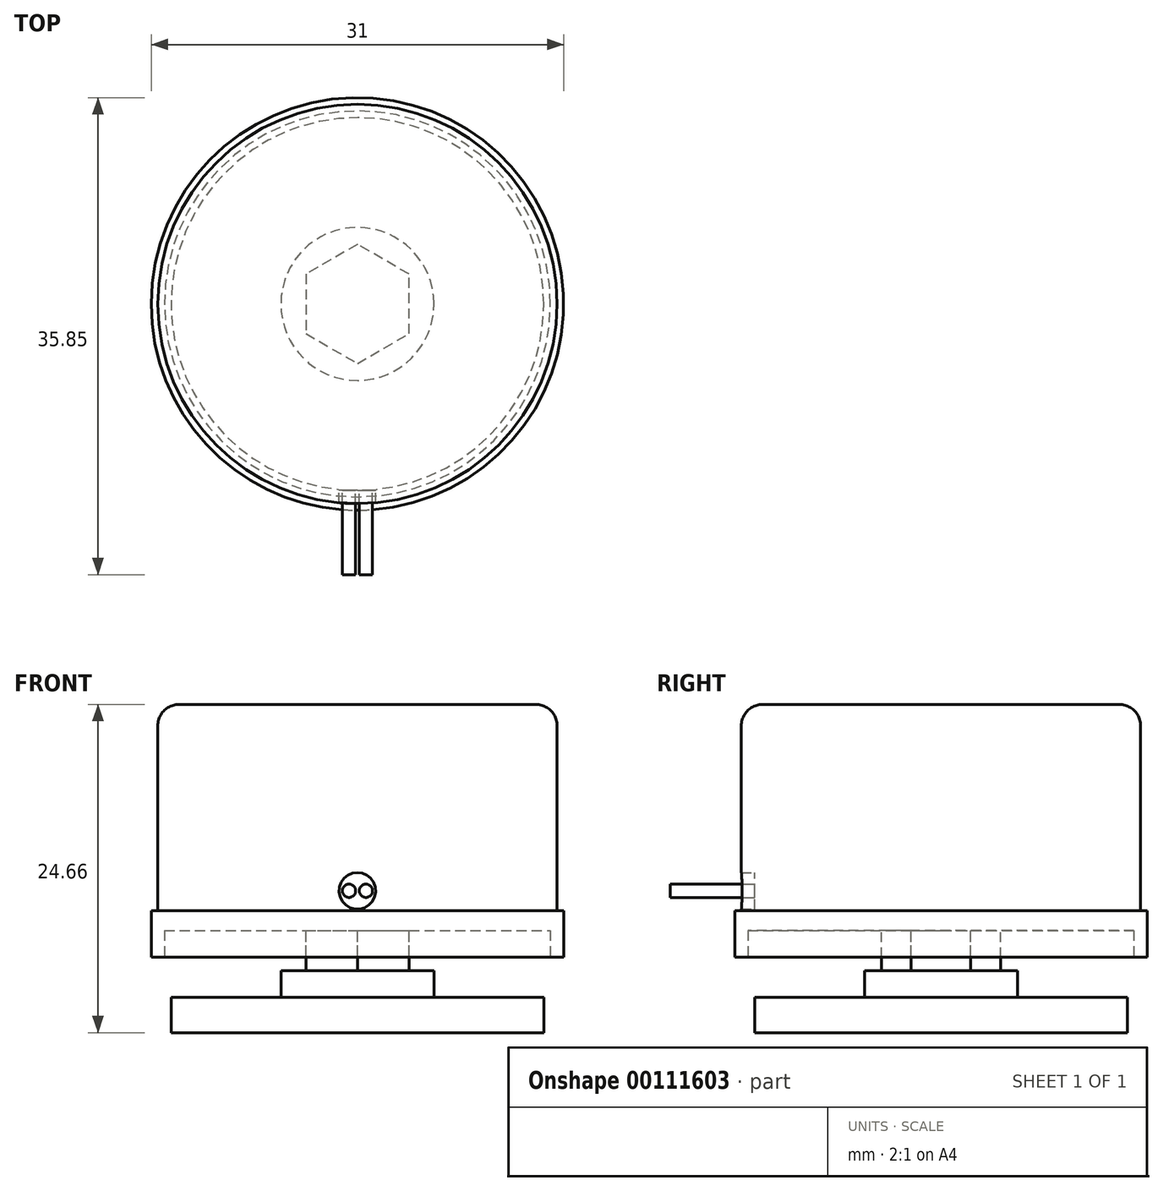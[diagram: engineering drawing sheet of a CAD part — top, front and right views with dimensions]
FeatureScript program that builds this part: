
annotation { "Feature Type Name" : "Feature", "Feature Type Description" : "" }
export const myFeature = defineFeature(function(context is Context, id is Id, definition is map)
    precondition{}
    {
        {
            var Q0;
            Q0=qCreatedBy(makeId("Top.planeOp"),FACE);
            var sketch = newSketch(context, id + "F0", { "sketchPlane" : qUnion([Q0])});
            skCircle(sketch, "E0", {"center": v(0, 0) * mm, "radius": 15 * mm});
            skSolve(sketch);
        }
        {
            var Q0;
            Q0 = qSketchRegion(id + "F0", true);
            extrude(context, id + "F1", {"entities" : qUnion([Q0]), "depth" : 19 * mm});
        }
        {
            var Q0;
            Q0=makeQuery(id+"F1.opExtrude","CAP_EDGE",EDGE,{"disambiguationData":[OSD([sQuery(id+"F0.wireOp",EDGE,"E0")])],"isStart":false});
            fillet(context, id + "F2", {"entities" : qUnion([Q0]), "radius" : 1.59 * mm, "tangentPropagation" : true, "allowEdgeOverflow" : false});
        }
        {
            var Q0;
            Q0=makeQuery(id+"F1.opExtrude","CAP_FACE",FACE,{"disambiguationData":[OSD([sQuery(id+"F0.wireOp",EDGE,"E0")])],"isStart":true});
            var sketch = newSketch(context, id + "F3", { "sketchPlane" : qUnion([Q0])});
            skCircle(sketch, "E1", {"center": v(0, 0) * mm, "radius": 15.5 * mm});
            skSolve(sketch);
        }
        {
            var Q0;
            Q0=makeQuery(id+"F3.imprint","IMPRINT",FACE,{"disambiguationData":[TD([[makeQuery(id+"F3.imprint","IMPRINT",EDGE,{"derivedFrom":sQuery(id+"F3.wireOp",EDGE,"E1")}),1.0]])]});
            extrude(context, id + "F4", {"entities" : qUnion([Q0]), "operationType" : NewBodyOperationType.ADD, "oppositeDirection" : true, "depth" : 3.5 * mm});
        }
        {
            var Q0;
            {var subQ0=sQuery(id+"F0.wireOp",EDGE,"E0");Q0=makeQuery(id+"F4.boolean.opBoolean","MERGE",FACE,{"derivedFrom":[makeQuery(id+"F1.opExtrude","CAP_FACE",FACE,{"disambiguationData":[OSD([subQ0])],"isStart":true}),makeQuery(id+"F4.opExtrude","CAP_FACE",FACE,{"disambiguationData":[OSD([subQ0,sQuery(id+"F3.wireOp",EDGE,"E1")])],"isStart":true})]});}
            var sketch = newSketch(context, id + "F5", { "sketchPlane" : qUnion([Q0])});
            skCircle(sketch, "E2", {"center": v(0, 0) * mm, "radius": 14.5 * mm});
            skSolve(sketch);
        }
        {
            var Q0;
            Q0=makeQuery(id+"F5.imprint","IMPRINT",FACE,{"disambiguationData":[TD([[makeQuery(id+"F5.imprint","IMPRINT",EDGE,{"derivedFrom":sQuery(id+"F5.wireOp",EDGE,"E2")}),1.0]])]});
            extrude(context, id + "F6", {"entities" : qUnion([Q0]), "operationType" : NewBodyOperationType.REMOVE, "oppositeDirection" : true, "depth" : 2 * mm});
        }
        {
            var Q0;
            Q0=makeQuery(id+"F6.boolean.opBoolean","COPY",FACE,{"derivedFrom":makeQuery(id+"F6.opExtrude","CAP_FACE",FACE,{"disambiguationData":[OSD([sQuery(id+"F5.wireOp",EDGE,"E2")])],"isStart":false})});
            var sketch = newSketch(context, id + "F7", { "sketchPlane" : qUnion([Q0])});
            skCircle(sketch, "E3.cCircle", {"center": v(0, 0) * mm, "radius": 3.88 * mm, "construction": true});
            skLineSegment(sketch, "E3.0", {"start": v(-3.87, 2.24) * mm, "end": v(0, 4.47) * mm});
            skLineSegment(sketch, "E3.1", {"start": v(0, 4.47) * mm, "end": v(3.88, 2.24) * mm});
            skLineSegment(sketch, "E3.2", {"start": v(3.88, 2.24) * mm, "end": v(3.88, -2.24) * mm});
            skLineSegment(sketch, "E3.3", {"start": v(3.88, -2.24) * mm, "end": v(0, -4.47) * mm});
            skLineSegment(sketch, "E3.4", {"start": v(0, -4.47) * mm, "end": v(-3.88, -2.24) * mm});
            skLineSegment(sketch, "E3.5", {"start": v(-3.88, -2.24) * mm, "end": v(-3.87, 2.24) * mm});
            skPoint(sketch, "E3.0.midPoint", {"position": v(-1.94, 3.36) * mm});
            skSolve(sketch);
        }
        {
            var Q0;
            Q0=makeQuery(id+"F7.imprint","IMPRINT",FACE,{"disambiguationData":[TD([[makeQuery(id+"F7.imprint","IMPRINT",EDGE,{"derivedFrom":sQuery(id+"F7.wireOp",EDGE,"E3.0")}),-1.0]])]});
            extrude(context, id + "F8", {"entities" : qUnion([Q0]), "operationType" : NewBodyOperationType.ADD, "depth" : 3 * mm});
        }
        {
            var Q0;
            Q0=makeQuery(id+"F8.opExtrude","CAP_FACE",FACE,{"disambiguationData":[OSD([sQuery(id+"F7.wireOp",EDGE,"E3.0"),sQuery(id+"F7.wireOp",EDGE,"E3.1"),sQuery(id+"F7.wireOp",EDGE,"E3.2"),sQuery(id+"F7.wireOp",EDGE,"E3.3"),sQuery(id+"F7.wireOp",EDGE,"E3.4"),sQuery(id+"F7.wireOp",EDGE,"E3.5")])],"isStart":false});
            var sketch = newSketch(context, id + "F9", { "sketchPlane" : qUnion([Q0])});
            skCircle(sketch, "E4", {"center": v(0, 0) * mm, "radius": 5.75 * mm});
            skSolve(sketch);
        }
        {
            var Q0;
            Q0=makeQuery(id+"F9.imprint","IMPRINT",FACE,{"disambiguationData":[TD([[makeQuery(id+"F9.imprint","IMPRINT",EDGE,{"derivedFrom":makeQuery(id+"F8.opExtrude","CAP_EDGE",EDGE,{"disambiguationData":[OSD([sQuery(id+"F7.wireOp",EDGE,"E3.0")])],"isStart":false})}),-1.0]])]});
            var Q1;
            Q1=makeQuery(id+"F9.imprint","IMPRINT",FACE,{"disambiguationData":[TD([[makeQuery(id+"F9.imprint","IMPRINT",EDGE,{"derivedFrom":sQuery(id+"F9.wireOp",EDGE,"E4")}),1.0]])]});
            extrude(context, id + "F10", {"entities" : qUnion([Q0, Q1]), "operationType" : NewBodyOperationType.ADD, "depth" : 2 * mm});
        }
        {
            var Q0;
            Q0=makeQuery(id+"F10.opExtrude","CAP_FACE",FACE,{"disambiguationData":[OSD([sQuery(id+"F9.wireOp",EDGE,"E4")])],"isStart":false});
            var sketch = newSketch(context, id + "F11", { "sketchPlane" : qUnion([Q0])});
            skCircle(sketch, "E5", {"center": v(0, 0) * mm, "radius": 14 * mm});
            skSolve(sketch);
        }
        {
            var Q0;
            Q0=makeQuery(id+"F11.imprint","IMPRINT",FACE,{"disambiguationData":[TD([[makeQuery(id+"F11.imprint","IMPRINT",EDGE,{"derivedFrom":sQuery(id+"F11.wireOp",EDGE,"E5")}),1.0]])]});
            var Q1;
            Q1=makeQuery(id+"F11.imprint","IMPRINT",FACE,{"disambiguationData":[TD([[makeQuery(id+"F11.imprint","IMPRINT",EDGE,{"derivedFrom":makeQuery(id+"F10.opExtrude","CAP_EDGE",EDGE,{"disambiguationData":[OSD([sQuery(id+"F9.wireOp",EDGE,"E4")])],"isStart":false})}),1.0]])]});
            extrude(context, id + "F12", {"entities" : qUnion([Q0, Q1]), "operationType" : NewBodyOperationType.ADD, "depth" : 2.66 * mm});
        }
        {
            var Q0;
            Q0=qCreatedBy(makeId("Front.planeOp"),FACE);
            var sketch = newSketch(context, id + "F13", { "sketchPlane" : qUnion([Q0])});
            skCircle(sketch, "E6", {"center": v(0, 5) * mm, "radius": 1.38 * mm});
            skSolve(sketch);
        }
        {
            var Q0;
            Q0 = qSketchRegion(id + "F13", true);
            extrude(context, id + "F14", {"entities" : qUnion([Q0]), "operationType" : NewBodyOperationType.REMOVE, "depth" : 25.4 * mm, "hasSecondDirection" : true, "secondDirectionOppositeDirection" : false, "secondDirectionDepth" : 14 * mm});
        }
        {
            var Q0;
            Q0=makeQuery(id+"F14.boolean.opBoolean","COPY",FACE,{"derivedFrom":makeQuery(id+"F14.opExtrude","CAP_FACE",FACE,{"disambiguationData":[OSD([sQuery(id+"F13.wireOp",EDGE,"E6")])],"isStart":true})});
            var sketch = newSketch(context, id + "F15", { "sketchPlane" : qUnion([Q0])});
            skCircle(sketch, "E7", {"center": v(-0.64, 5) * mm, "radius": 0.5 * mm});
            skCircle(sketch, "E8", {"center": v(0.63, 5) * mm, "radius": 0.5 * mm});
            skCircle(sketch, "E9.0", {"center": v(0, 5) * mm, "radius": 1.38 * mm});
            skLineSegment(sketch, "E10", {"start": v(-0.64, 5) * mm, "end": v(0.63, 5) * mm, "construction": true});
            skSolve(sketch);
        }
        {
            var Q0;
            Q0=makeQuery(id+"F15.imprint","IMPRINT",FACE,{"disambiguationData":[TD([[makeQuery(id+"F15.imprint","IMPRINT",EDGE,{"derivedFrom":sQuery(id+"F15.wireOp",EDGE,"E7")}),1.0]])]});
            var Q1;
            Q1=makeQuery(id+"F15.imprint","IMPRINT",FACE,{"disambiguationData":[TD([[makeQuery(id+"F15.imprint","IMPRINT",EDGE,{"derivedFrom":sQuery(id+"F15.wireOp",EDGE,"E8")}),1.0]])]});
            extrude(context, id + "F16", {"entities" : qUnion([Q0, Q1]), "operationType" : NewBodyOperationType.ADD, "depth" : 6.35 * mm});
        }
    });
